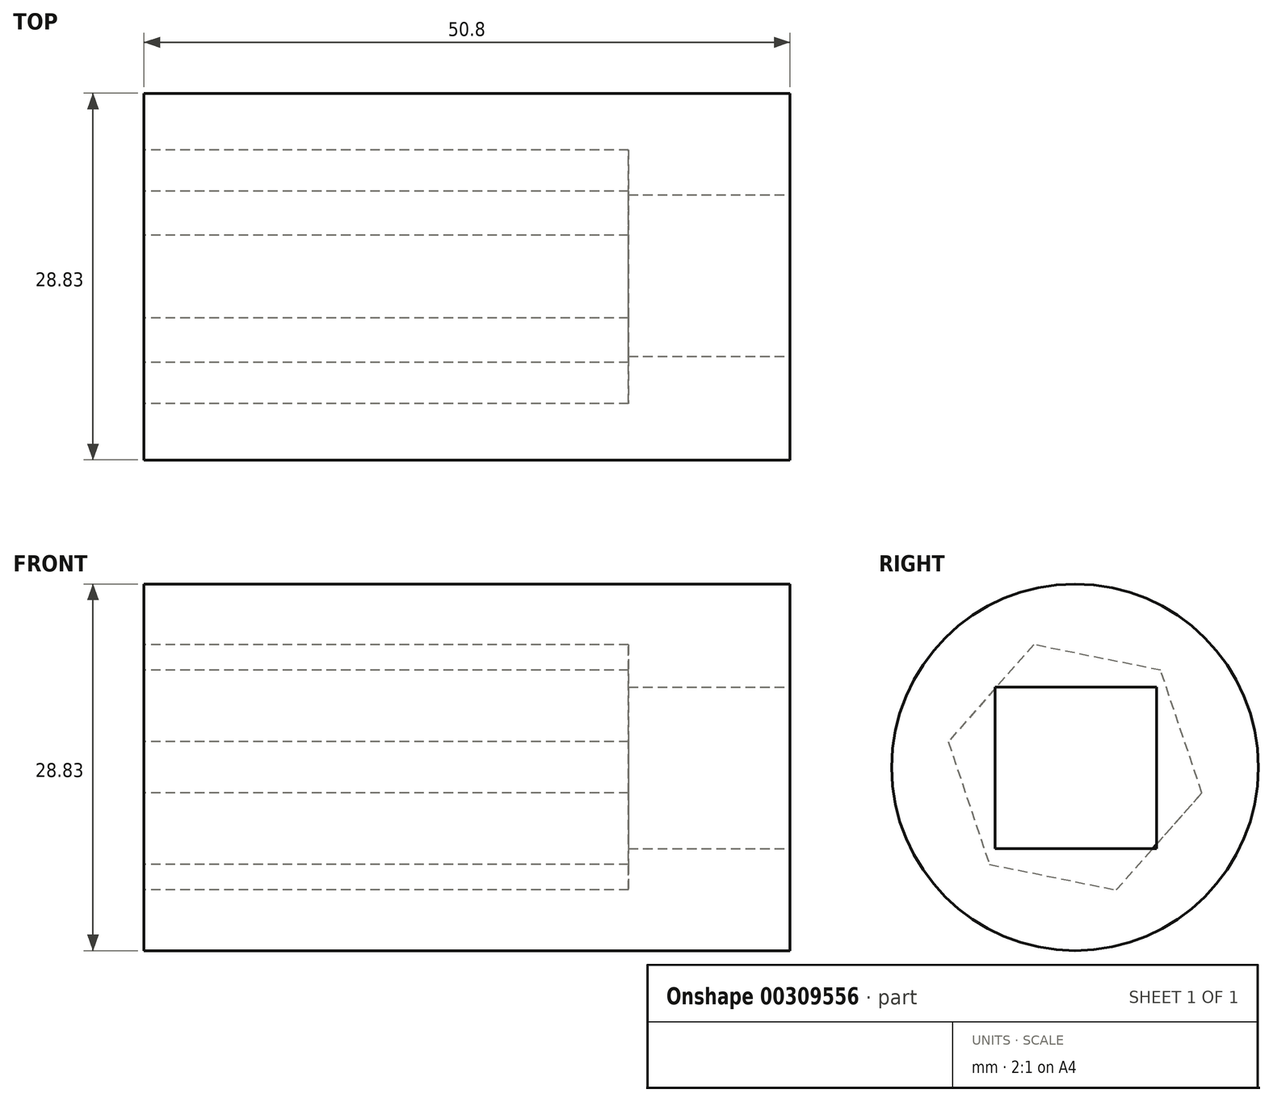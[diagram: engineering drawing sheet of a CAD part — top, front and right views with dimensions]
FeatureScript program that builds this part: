
annotation { "Feature Type Name" : "Feature", "Feature Type Description" : "" }
export const myFeature = defineFeature(function(context is Context, id is Id, definition is map)
    precondition{}
    {
        {
            var Q0;
            Q0=qCreatedBy(makeId("Right.planeOp"),FACE);
            var sketch = newSketch(context, id + "F0", { "sketchPlane" : qUnion([Q0])});
            skCircle(sketch, "E0", {"center": v(-56.14, 5.55) * mm, "radius": 14.41 * mm});
            skSolve(sketch);
        }
        {
            var Q0;
            Q0=makeQuery(id+"F0.imprint","IMPRINT",FACE,{"disambiguationData":[TD([[makeQuery(id+"F0.imprint","IMPRINT",EDGE,{"derivedFrom":sQuery(id+"F0.wireOp",EDGE,"E0")}),1.0]])]});
            extrude(context, id + "F1", {"entities" : qUnion([Q0]), "oppositeDirection" : true, "depth" : 50.8 * mm});
        }
        {
            var Q0;
            Q0=makeQuery(id+"F1.opExtrude","CAP_FACE",FACE,{"disambiguationData":[OSD([sQuery(id+"F0.wireOp",EDGE,"E0")])],"isStart":true});
            var sketch = newSketch(context, id + "F2", { "sketchPlane" : qUnion([Q0])});
            skLineSegment(sketch, "E1.bottom", {"start": v(-62.42, 11.85) * mm, "end": v(-49.72, 11.85) * mm});
            skLineSegment(sketch, "E1.top", {"start": v(-62.42, -0.85) * mm, "end": v(-49.72, -0.85) * mm});
            skLineSegment(sketch, "E1.left", {"start": v(-62.42, 11.85) * mm, "end": v(-62.42, -0.85) * mm});
            skLineSegment(sketch, "E1.right", {"start": v(-49.72, 11.85) * mm, "end": v(-49.72, -0.85) * mm});
            skSolve(sketch);
        }
        {
            var Q0;
            Q0=makeQuery(id+"F2.imprint","IMPRINT",FACE,{"disambiguationData":[TD([[makeQuery(id+"F2.imprint","IMPRINT",EDGE,{"derivedFrom":sQuery(id+"F2.wireOp",EDGE,"E1.bottom")}),-1.0]])]});
            extrude(context, id + "F3", {"entities" : qUnion([Q0]), "operationType" : NewBodyOperationType.REMOVE, "oppositeDirection" : true, "depth" : 12.7 * mm});
        }
        {
            var Q0;
            Q0=makeQuery(id+"F1.opExtrude","CAP_FACE",FACE,{"disambiguationData":[OSD([sQuery(id+"F0.wireOp",EDGE,"E0")])],"isStart":false});
            var sketch = newSketch(context, id + "F4", { "sketchPlane" : qUnion([Q0])});
            skCircle(sketch, "E2.cCircle", {"center": v(56.14, 5.55) * mm, "radius": 8.8 * mm, "construction": true});
            skLineSegment(sketch, "E2.0", {"start": v(66.11, 7.56) * mm, "end": v(62.87, -2.08) * mm});
            skLineSegment(sketch, "E2.1", {"start": v(62.87, -2.08) * mm, "end": v(52.9, -4.09) * mm});
            skLineSegment(sketch, "E2.2", {"start": v(52.9, -4.09) * mm, "end": v(46.17, 3.54) * mm});
            skLineSegment(sketch, "E2.3", {"start": v(46.17, 3.54) * mm, "end": v(49.41, 13.18) * mm});
            skLineSegment(sketch, "E2.4", {"start": v(49.41, 13.18) * mm, "end": v(59.38, 15.2) * mm});
            skLineSegment(sketch, "E2.5", {"start": v(59.38, 15.2) * mm, "end": v(66.11, 7.56) * mm});
            skPoint(sketch, "E2.0.midPoint", {"position": v(64.49, 2.74) * mm});
            skSolve(sketch);
        }
        {
            var Q0;
            Q0=makeQuery(id+"F4.imprint","IMPRINT",FACE,{"disambiguationData":[TD([[makeQuery(id+"F4.imprint","IMPRINT",EDGE,{"derivedFrom":sQuery(id+"F4.wireOp",EDGE,"E2.0")}),-1.0]])]});
            var Q1;
            Q1=makeQuery(id+"F3.boolean.opBoolean","COPY",FACE,{"derivedFrom":makeQuery(id+"F3.opExtrude","CAP_FACE",FACE,{"disambiguationData":[OSD([sQuery(id+"F2.wireOp",EDGE,"E1.bottom"),sQuery(id+"F2.wireOp",EDGE,"E1.top"),sQuery(id+"F2.wireOp",EDGE,"E1.left"),sQuery(id+"F2.wireOp",EDGE,"E1.right")])],"isStart":false})});
            extrude(context, id + "F5", {"entities" : qUnion([Q0]), "operationType" : NewBodyOperationType.REMOVE, "endBound" : BoundingType.UP_TO_SURFACE, "oppositeDirection" : true, "endBoundEntityFace" : qUnion([Q1]), "depth" : 25.4 * mm});
        }
    });
